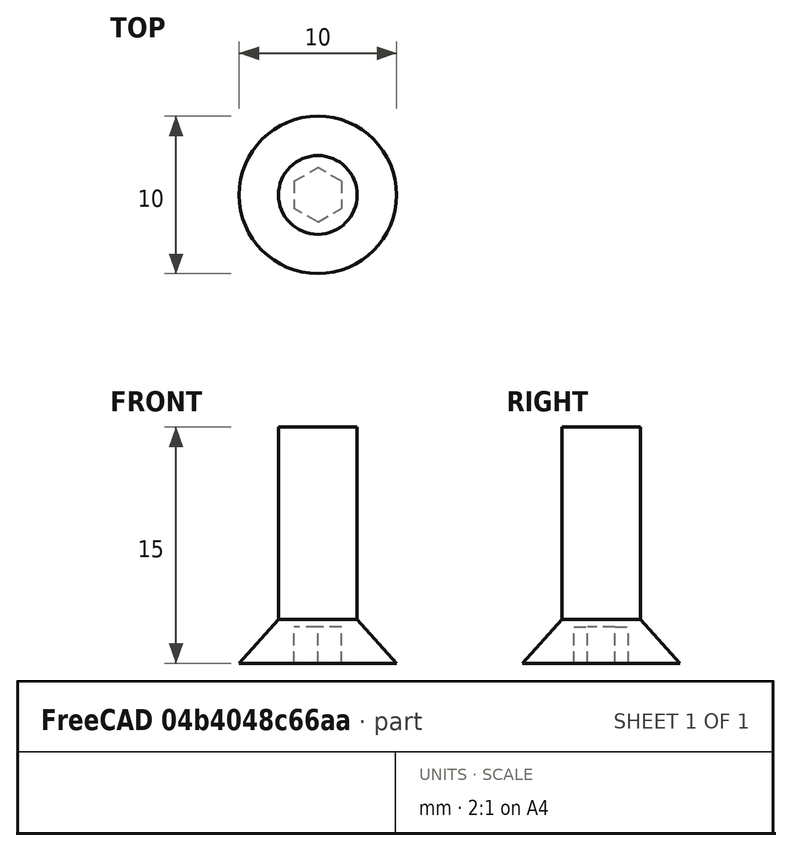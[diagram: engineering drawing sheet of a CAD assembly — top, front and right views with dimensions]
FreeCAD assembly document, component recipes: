
FREECAD ASSEMBLY — COMPONENT RECIPES ("dbox_asm")

This assembly document has 117 components, labeled P0..P116 below (a component is one placed body or linked part). 16 of them carry a construction recipe — the FreeCAD feature program that regenerates the part from scratch, quoted from this document or its linked companion documents; the rest are supplied as boundary geometry only. No exploded tour is included for this assembly.
COMPONENT P0 — recipe-attached ("corner1", a linked part whose construction recipe lives in a companion FreeCAD document of the same project; that document's serialized recipe follows).
Construction recipe (the companion document, serialized — sketch geometry with constraints, then the solid features built on it; lengths are millimeters unless a unit is written):

FCSTD DOCUMENT  (FreeCAD 1.0R39109 (Git))
Label: 2020-corner-bracket
License: All rights reserved
LicenseURL: http://en.wikipedia.org/wiki/All_rights_reserved
objects: Sketcher::SketchObject×5, PartDesign::Pocket×3, PartDesign::Pad×2, PartDesign::PolarPattern×1, PartDesign::Chamfer×1, PartDesign::Body×1, App::Part×1
note: 31 computed .brp shape members not serialized (recipe doc carries the construction recipe); baked Part::Feature solids carry a one-line shape summary decoded from their .brp

FEATURE [Sketcher::SketchObject] Sketch
  ArcFitTolerance = 0
  AttachmentSupport = -> [XZ_Plane001]
  FullyConstrained = true
  MakeInternals = false
  MapMode = 5
  Placement = pos=(0,0,0) rot=(1,0,0;1.5708rad)
  sketch-geometry (5):
    g0: LineSegment StartX=-10 StartY=10 StartZ=0 EndX=-10 EndY=-10 EndZ=0
    g1: LineSegment StartX=-10 StartY=-10 StartZ=0 EndX=10 EndY=-10 EndZ=0
    g2: LineSegment StartX=10 StartY=-10 StartZ=0 EndX=10 EndY=-7 EndZ=0
    g3: LineSegment StartX=10 StartY=-7 StartZ=0 EndX=-7 EndY=10 EndZ=0
    g4: LineSegment StartX=-7 StartY=10 StartZ=0 EndX=-10 EndY=10 EndZ=0
  constraints (13):
    c: Coincident(g0,g1)
    c: Coincident(g1,g2)
    c: Vertical(g2)
    c: Coincident(g2,g3)
    c: Coincident(g3,g4)
    c: Coincident(g4,g0)
    c: Horizontal(g4)
    c: DistanceX(g1,g1) = 20
    c: DistanceY(g2,g2) = 3
    c: Equal(g2,g4)
    c: Equal(g1,g0)
    c: Symmetric(g0,g0,g-1)
    c: Symmetric(g0,g1,g-2)
FEATURE [PartDesign::Pad] Pad
  Direction = (0,-1,2e-16)
  Length = 17
  Length2 = 10
  Midplane = true
  Placement = pos=(0,0,0) rot=(1,0,0;1.5708rad)
  Profile = -> Sketch
  ReferenceAxis = -> Sketch [N_Axis]
  Suppressed = false
  Type = 0
FEATURE [Sketcher::SketchObject] Sketch001
  ArcFitTolerance = 0
  AttachmentSupport = -> [Pad]
  FullyConstrained = true
  MakeInternals = false
  MapMode = 5
  Placement = pos=(-10,0,0) rot=(0.707107,0,-0.707107;3.14159rad)
  sketch-geometry (4):
    g0: ArcOfCircle CenterX=-1.5 CenterY=-2e-16 CenterZ=0 NormalX=0 NormalY=0 NormalZ=1 AngleXU=0 Radius=2.9 StartAngle=1.5708 EndAngle=4.71239
    g1: ArcOfCircle CenterX=1.5 CenterY=-2e-16 CenterZ=0 NormalX=0 NormalY=0 NormalZ=1 AngleXU=0 Radius=2.9 StartAngle=4.71239 EndAngle=7.85398
    g2: LineSegment StartX=-1.5 StartY=-2.9 StartZ=0 EndX=1.5 EndY=-2.9 EndZ=0
    g3: LineSegment StartX=1.5 StartY=2.9 StartZ=0 EndX=-1.5 EndY=2.9 EndZ=0
  constraints (9):
    c: Tangent(g0,g2) = -1.5708
    c: Tangent(g2,g1) = -1.5708
    c: Tangent(g1,g3) = -1.5708
    c: Tangent(g3,g0) = -1.5708
    c: Equal(g0,g1)
    c: DistanceX(g0,g1) = 3
    c: Radius(g0) = 2.9
    c: Symmetric(g1,g0,g-2)
    c: Symmetric(g1,g1,g-1)
FEATURE [PartDesign::Pocket] Pocket
  BaseFeature = -> Pad
  Direction = (1,0,2e-16)
  Length = 3
  Length2 = 5
  Placement = pos=(0,0,0) rot=(1,0,0;1.5708rad)
  Profile = -> Sketch001
  ReferenceAxis = -> Sketch001 [N_Axis]
  Suppressed = false
  Type = 0
FEATURE [Sketcher::SketchObject] Sketch002
  ArcFitTolerance = 0
  AttachmentSupport = -> [Pocket]
  FullyConstrained = true
  MakeInternals = false
  MapMode = 5
  Placement = pos=(0,-4.4e-15,-10) rot=(1,0,0;3.14159rad)
  sketch-geometry (4):
    g0: ArcOfCircle CenterX=-1.5 CenterY=-1e-16 CenterZ=0 NormalX=0 NormalY=0 NormalZ=1 AngleXU=0 Radius=2.9 StartAngle=1.5708 EndAngle=4.71239
    g1: ArcOfCircle CenterX=1.5 CenterY=-1e-16 CenterZ=0 NormalX=0 NormalY=0 NormalZ=1 AngleXU=0 Radius=2.9 StartAngle=4.71239 EndAngle=7.85398
    g2: LineSegment StartX=-1.5 StartY=-2.9 StartZ=0 EndX=1.5 EndY=-2.9 EndZ=0
    g3: LineSegment StartX=1.5 StartY=2.9 StartZ=0 EndX=-1.5 EndY=2.9 EndZ=0
  constraints (9):
    c: Tangent(g0,g2) = -1.5708
    c: Tangent(g2,g1) = -1.5708
    c: Tangent(g1,g3) = -1.5708
    c: Tangent(g3,g0) = -1.5708
    c: Equal(g0,g1)
    c: DistanceX(g0,g1) = 3
    c: Radius(g0) = 2.9
    c: Symmetric(g1,g0,g-2)
    c: Symmetric(g1,g1,g-1)
FEATURE [PartDesign::Pocket] Pocket001
  BaseFeature = -> Pocket
  Direction = (0,0,1)
  Length = 3
  Length2 = 5
  Placement = pos=(0,0,0) rot=(1,0,0;1.5708rad)
  Profile = -> Sketch002
  ReferenceAxis = -> Sketch002 [N_Axis]
  Suppressed = false
  Type = 0
FEATURE [Sketcher::SketchObject] Sketch003
  ArcFitTolerance = 0
  AttachmentSupport = -> [Pocket001]
  ExternalGeometry = -> [Pocket001]
  FullyConstrained = true
  MakeInternals = false
  MapMode = 5
  Placement = pos=(0,0,-7) rot=(1,0,0;3.14159rad)
  sketch-geometry (4):
    g0: LineSegment StartX=-7 StartY=5.5 StartZ=0 EndX=10 EndY=5.5 EndZ=0
    g1: LineSegment StartX=10 StartY=5.5 StartZ=0 EndX=10 EndY=-5.5 EndZ=0
    g2: LineSegment StartX=10 StartY=-5.5 StartZ=0 EndX=-7 EndY=-5.5 EndZ=0
    g3: LineSegment StartX=-7 StartY=-5.5 StartZ=0 EndX=-7 EndY=5.5 EndZ=0
  constraints (11):
    c: Coincident(g0,g1)
    c: Coincident(g1,g2)
    c: Coincident(g2,g3)
    c: Coincident(g3,g0)
    c: Horizontal(g0)
    c: Horizontal(g2)
    c: Vertical(g3)
    c: DistanceY(g3,g3) = 11
    c: Symmetric(g1,g0,g-1)
    c: DistanceX(g0) = -7
    c: DistanceX(g0,g-3) = 0
FEATURE [PartDesign::Pocket] Pocket002
  BaseFeature = -> Pocket001
  Direction = (0,0,1)
  Length = 5
  Length2 = 5
  Placement = pos=(0,0,0) rot=(1,0,0;1.5708rad)
  Profile = -> Sketch003
  ReferenceAxis = -> Sketch003 [N_Axis]
  Suppressed = false
  Type = 1
FEATURE [Sketcher::SketchObject] Sketch004
  ArcFitTolerance = 0
  AttachmentSupport = -> [Pocket002]
  ExternalGeometry = -> [Pocket002]
  FullyConstrained = true
  MakeInternals = false
  MapMode = 5
  Placement = pos=(-10,0,0) rot=(0.707107,0,-0.707107;3.14159rad)
  sketch-geometry (8):
    g0: LineSegment StartX=-8.5 StartY=2 StartZ=0 EndX=-7 EndY=2 EndZ=0
    g1: LineSegment StartX=-7 StartY=2 StartZ=0 EndX=-7 EndY=-2 EndZ=0
    g2: LineSegment StartX=-7 StartY=-2 StartZ=0 EndX=-8.5 EndY=-2 EndZ=0
    g3: LineSegment StartX=-8.5 StartY=-2 StartZ=0 EndX=-8.5 EndY=2 EndZ=0
    g4: LineSegment StartX=7 StartY=2 StartZ=0 EndX=8.5 EndY=2 EndZ=0
    g5: LineSegment StartX=8.5 StartY=2 StartZ=0 EndX=8.5 EndY=-2 EndZ=0
    g6: LineSegment StartX=8.5 StartY=-2 StartZ=0 EndX=7 EndY=-2 EndZ=0
    g7: LineSegment StartX=7 StartY=-2 StartZ=0 EndX=7 EndY=2 EndZ=0
  constraints (23):
    c: Coincident(g0,g1)
    c: Coincident(g1,g2)
    c: Coincident(g2,g3)
    c: Coincident(g3,g0)
    c: Horizontal(g0)
    c: Horizontal(g2)
    c: Vertical(g1)
    c: Vertical(g3)
    c: Coincident(g4,g5)
    c: Coincident(g5,g6)
    c: Coincident(g6,g7)
    c: Coincident(g7,g4)
    c: Horizontal(g4)
    c: Horizontal(g6)
    c: Vertical(g7)
    c: Equal(g5,g1)
    c: Equal(g2,g6)
    c: DistanceX(g0,g0) = 1.5
    c: Horizontal(g1,g6)
    c: Symmetric(g5,g4,g-1)
    c: DistanceX(g4,g-3) = 1.5
    c: DistanceY(g1,g1) = 4
    c: DistanceX(g-4,g0) = 1.5
FEATURE [PartDesign::Pad] Pad001
  BaseFeature = -> Pocket002
  Direction = (-1,0,-2e-16)
  Length = 1
  Length2 = 10
  Placement = pos=(0,0,0) rot=(1,0,0;1.5708rad)
  Profile = -> Sketch004
  ReferenceAxis = -> Sketch004 [N_Axis]
  Suppressed = false
  Type = 0
FEATURE [PartDesign::PolarPattern] PolarPattern
  Angle = 90
  Axis = -> Y_Axis001
  BaseFeature = -> Pad001
  Mode = 0
  Occurrences = 2
  Offset = 120
  Originals = -> [Pad001]
  Placement = pos=(0,0,0) rot=(1,0,0;1.5708rad)
  Reversed = true
  Suppressed = false
  TransformMode = 0
FEATURE [PartDesign::Chamfer] Chamfer
  Angle = 45
  Base = -> PolarPattern [Edge48,Edge45,Edge64,Edge61,Edge80,Edge77,Edge96,Edge93]
  BaseFeature = -> PolarPattern
  ChamferType = 0
  FlipDirection = false
  Placement = pos=(0,0,0) rot=(1,0,0;1.5708rad)
  Size = 0.25
  Size2 = 1
  SupportTransform = false
  Suppressed = false
  UseAllEdges = false
FEATURE [PartDesign::Body] Body
  AllowCompound = false
  Group = -> [Sketch,Pad,Sketch001,Pocket,Sketch002,Pocket001,Sketch003,Pocket002,Sketch004,Pad001,PolarPattern,Chamfer]
  Origin = -> Origin001
  Tip = -> Chamfer
FEATURE [App::Part] Part  label="Part_Bracket"
  Group = -> [Body]
  Origin = -> Origin
COMPONENT P1 — same part as P0; its construction recipe is shown at P0.
COMPONENT P2 — same part as P0; its construction recipe is shown at P0.
COMPONENT P3 — same part as P0; its construction recipe is shown at P0.
COMPONENT P4 — same part as P0; its construction recipe is shown at P0.
COMPONENT P5 — same part as P0; its construction recipe is shown at P0.
COMPONENT P6 — same part as P0; its construction recipe is shown at P0.
COMPONENT P7 — same part as P0; its construction recipe is shown at P0.
COMPONENT P8 — same part as P0; its construction recipe is shown at P0.
COMPONENT P9 — same part as P0; its construction recipe is shown at P0.
COMPONENT P10 — same part as P0; its construction recipe is shown at P0.
COMPONENT P11 — same part as P0; its construction recipe is shown at P0.
COMPONENT P12 — same part as P0; its construction recipe is shown at P0.
COMPONENT P13 — same part as P0; its construction recipe is shown at P0.
COMPONENT P14 — same part as P0; its construction recipe is shown at P0.
COMPONENT P15 — same part as P0; its construction recipe is shown at P0.
COMPONENT P16 — geometry summary ("Hex screw M5 10.008"; no construction recipe available for this part):
  bounding box: 14.0 x 8.5 x 8.5 mm
  tessellated surface: 664 triangles
  volume: 423 mm^3 (42% of its bounding box)
  symmetry: revolution-symmetric about the z axis through its bounding-box center; mirror-symmetric across its x mid-plane, y mid-plane
COMPONENT P17 — geometry summary ("Hex screw M5 10.009"; no construction recipe available for this part):
  bounding box: 14.0 x 8.5 x 8.5 mm
  tessellated surface: 664 triangles
  volume: 423 mm^3 (42% of its bounding box)
  symmetry: revolution-symmetric about the z axis through its bounding-box center; mirror-symmetric across its x mid-plane, y mid-plane
COMPONENT P18 — geometry summary ("Hex screw M5 10.010"; no construction recipe available for this part):
  bounding box: 14.0 x 8.5 x 8.5 mm
  tessellated surface: 664 triangles
  volume: 423 mm^3 (42% of its bounding box)
  symmetry: revolution-symmetric about the z axis through its bounding-box center; mirror-symmetric across its x mid-plane, y mid-plane
COMPONENT P19 — geometry summary ("Hex screw M5 10.011"; no construction recipe available for this part):
  bounding box: 14.0 x 8.5 x 8.5 mm
  tessellated surface: 664 triangles
  volume: 423 mm^3 (42% of its bounding box)
  symmetry: revolution-symmetric about the z axis through its bounding-box center; mirror-symmetric across its x mid-plane, y mid-plane
COMPONENT P20 — geometry summary ("Hex screw M5 10.012"; no construction recipe available for this part):
  bounding box: 14.0 x 8.5 x 8.5 mm
  tessellated surface: 664 triangles
  volume: 423 mm^3 (42% of its bounding box)
  symmetry: revolution-symmetric about the z axis through its bounding-box center; mirror-symmetric across its x mid-plane, y mid-plane
COMPONENT P21 — geometry summary ("Hex screw M5 10.013"; no construction recipe available for this part):
  bounding box: 14.0 x 8.5 x 8.5 mm
  tessellated surface: 664 triangles
  volume: 423 mm^3 (42% of its bounding box)
  symmetry: revolution-symmetric about the z axis through its bounding-box center; mirror-symmetric across its x mid-plane, y mid-plane
COMPONENT P22 — geometry summary ("Hex screw M5 10.014"; no construction recipe available for this part):
  bounding box: 14.0 x 8.5 x 8.5 mm
  tessellated surface: 664 triangles
  volume: 423 mm^3 (42% of its bounding box)
  symmetry: revolution-symmetric about the z axis through its bounding-box center; mirror-symmetric across its x mid-plane, y mid-plane
COMPONENT P23 — geometry summary ("Hex screw M5 10.015"; no construction recipe available for this part):
  bounding box: 14.0 x 8.5 x 8.5 mm
  tessellated surface: 664 triangles
  volume: 423 mm^3 (42% of its bounding box)
  symmetry: revolution-symmetric about the z axis through its bounding-box center; mirror-symmetric across its x mid-plane, y mid-plane
COMPONENT P24 — geometry summary ("Hex screw M5 10.016"; no construction recipe available for this part):
  bounding box: 14.0 x 8.5 x 8.5 mm
  tessellated surface: 664 triangles
  volume: 423 mm^3 (42% of its bounding box)
  symmetry: revolution-symmetric about the z axis through its bounding-box center; mirror-symmetric across its x mid-plane, y mid-plane
COMPONENT P25 — geometry summary ("Hex screw M5 10.017"; no construction recipe available for this part):
  bounding box: 14.0 x 8.5 x 8.5 mm
  tessellated surface: 664 triangles
  volume: 423 mm^3 (42% of its bounding box)
  symmetry: revolution-symmetric about the z axis through its bounding-box center; mirror-symmetric across its x mid-plane, y mid-plane
COMPONENT P26 — geometry summary ("Hex screw M5 10.018"; no construction recipe available for this part):
  bounding box: 14.0 x 8.5 x 8.5 mm
  tessellated surface: 664 triangles
  volume: 423 mm^3 (42% of its bounding box)
  symmetry: revolution-symmetric about the z axis through its bounding-box center; mirror-symmetric across its x mid-plane, y mid-plane
COMPONENT P27 — geometry summary ("Hex screw M5 10.019"; no construction recipe available for this part):
  bounding box: 14.0 x 8.5 x 8.5 mm
  tessellated surface: 664 triangles
  volume: 423 mm^3 (42% of its bounding box)
  symmetry: revolution-symmetric about the z axis through its bounding-box center; mirror-symmetric across its x mid-plane, y mid-plane
COMPONENT P28 — geometry summary ("Hex screw M5 10.020"; no construction recipe available for this part):
  bounding box: 14.0 x 8.5 x 8.5 mm
  tessellated surface: 664 triangles
  volume: 423 mm^3 (42% of its bounding box)
  symmetry: revolution-symmetric about the z axis through its bounding-box center; mirror-symmetric across its x mid-plane, y mid-plane
COMPONENT P29 — geometry summary ("Hex screw M5 10.021"; no construction recipe available for this part):
  bounding box: 14.0 x 8.5 x 8.5 mm
  tessellated surface: 664 triangles
  volume: 423 mm^3 (42% of its bounding box)
  symmetry: revolution-symmetric about the z axis through its bounding-box center; mirror-symmetric across its x mid-plane, y mid-plane
COMPONENT P30 — geometry summary ("Hex screw M5 10.022"; no construction recipe available for this part):
  bounding box: 14.0 x 8.5 x 8.5 mm
  tessellated surface: 664 triangles
  volume: 423 mm^3 (42% of its bounding box)
  symmetry: revolution-symmetric about the z axis through its bounding-box center; mirror-symmetric across its x mid-plane, y mid-plane
COMPONENT P31 — geometry summary ("Hex screw M5 10.023"; no construction recipe available for this part):
  bounding box: 14.0 x 8.5 x 8.5 mm
  tessellated surface: 664 triangles
  volume: 423 mm^3 (42% of its bounding box)
  symmetry: revolution-symmetric about the z axis through its bounding-box center; mirror-symmetric across its x mid-plane, y mid-plane
COMPONENT P32 — geometry summary ("Hex screw M5 10.024"; no construction recipe available for this part):
  bounding box: 14.0 x 8.5 x 8.5 mm
  tessellated surface: 664 triangles
  volume: 423 mm^3 (42% of its bounding box)
  symmetry: revolution-symmetric about the z axis through its bounding-box center; mirror-symmetric across its x mid-plane, y mid-plane
COMPONENT P33 — geometry summary ("Hex screw M5 10.025"; no construction recipe available for this part):
  bounding box: 14.0 x 8.5 x 8.5 mm
  tessellated surface: 664 triangles
  volume: 423 mm^3 (42% of its bounding box)
  symmetry: revolution-symmetric about the z axis through its bounding-box center; mirror-symmetric across its x mid-plane, y mid-plane
COMPONENT P34 — geometry summary ("Hex screw M5 10.026"; no construction recipe available for this part):
  bounding box: 14.0 x 8.5 x 8.5 mm
  tessellated surface: 664 triangles
  volume: 423 mm^3 (42% of its bounding box)
  symmetry: revolution-symmetric about the z axis through its bounding-box center; mirror-symmetric across its x mid-plane, y mid-plane
COMPONENT P35 — geometry summary ("Hex screw M5 10.028"; no construction recipe available for this part):
  bounding box: 14.0 x 8.5 x 8.5 mm
  tessellated surface: 664 triangles
  volume: 423 mm^3 (42% of its bounding box)
  symmetry: revolution-symmetric about the z axis through its bounding-box center; mirror-symmetric across its x mid-plane, y mid-plane
COMPONENT P36 — geometry summary ("Hex screw M5 10.027"; no construction recipe available for this part):
  bounding box: 14.0 x 8.5 x 8.5 mm
  tessellated surface: 664 triangles
  volume: 423 mm^3 (42% of its bounding box)
  symmetry: revolution-symmetric about the z axis through its bounding-box center; mirror-symmetric across its x mid-plane, y mid-plane
COMPONENT P37 — geometry summary ("Hex screw M5 10.029"; no construction recipe available for this part):
  bounding box: 14.0 x 8.5 x 8.5 mm
  tessellated surface: 664 triangles
  volume: 423 mm^3 (42% of its bounding box)
  symmetry: revolution-symmetric about the z axis through its bounding-box center; mirror-symmetric across its x mid-plane, y mid-plane
COMPONENT P38 — geometry summary ("Hex screw M5 10.030"; no construction recipe available for this part):
  bounding box: 14.0 x 8.5 x 8.5 mm
  tessellated surface: 664 triangles
  volume: 423 mm^3 (42% of its bounding box)
  symmetry: revolution-symmetric about the z axis through its bounding-box center; mirror-symmetric across its x mid-plane, y mid-plane
COMPONENT P39 — geometry summary ("Hex screw M5 10.031"; no construction recipe available for this part):
  bounding box: 14.0 x 8.5 x 8.5 mm
  tessellated surface: 664 triangles
  volume: 423 mm^3 (42% of its bounding box)
  symmetry: revolution-symmetric about the z axis through its bounding-box center; mirror-symmetric across its x mid-plane, y mid-plane
COMPONENT P40 — geometry summary ("Hex screw M5 10.032"; no construction recipe available for this part):
  bounding box: 14.0 x 8.5 x 8.5 mm
  tessellated surface: 664 triangles
  volume: 423 mm^3 (42% of its bounding box)
  symmetry: revolution-symmetric about the z axis through its bounding-box center; mirror-symmetric across its x mid-plane, y mid-plane
COMPONENT P41 — geometry summary ("Hex screw M5 10.033"; no construction recipe available for this part):
  bounding box: 14.0 x 8.5 x 8.5 mm
  tessellated surface: 664 triangles
  volume: 423 mm^3 (42% of its bounding box)
  symmetry: revolution-symmetric about the z axis through its bounding-box center; mirror-symmetric across its x mid-plane, y mid-plane
COMPONENT P42 — geometry summary ("Hex screw M5 10.034"; no construction recipe available for this part):
  bounding box: 14.0 x 8.5 x 8.5 mm
  tessellated surface: 664 triangles
  volume: 423 mm^3 (42% of its bounding box)
  symmetry: revolution-symmetric about the z axis through its bounding-box center; mirror-symmetric across its x mid-plane, y mid-plane
COMPONENT P43 — geometry summary ("Hex screw M5 10.035"; no construction recipe available for this part):
  bounding box: 14.0 x 8.5 x 8.5 mm
  tessellated surface: 664 triangles
  volume: 423 mm^3 (42% of its bounding box)
  symmetry: revolution-symmetric about the z axis through its bounding-box center; mirror-symmetric across its x mid-plane, y mid-plane
COMPONENT P44 — geometry summary ("Hex screw M5 10.036"; no construction recipe available for this part):
  bounding box: 14.0 x 8.5 x 8.5 mm
  tessellated surface: 664 triangles
  volume: 423 mm^3 (42% of its bounding box)
  symmetry: revolution-symmetric about the z axis through its bounding-box center; mirror-symmetric across its x mid-plane, y mid-plane
COMPONENT P45 — geometry summary ("Hex screw M5 10.037"; no construction recipe available for this part):
  bounding box: 14.0 x 8.5 x 8.5 mm
  tessellated surface: 664 triangles
  volume: 423 mm^3 (42% of its bounding box)
  symmetry: revolution-symmetric about the z axis through its bounding-box center; mirror-symmetric across its x mid-plane, y mid-plane
COMPONENT P46 — geometry summary ("Hex screw M5 10.038"; no construction recipe available for this part):
  bounding box: 14.0 x 8.5 x 8.5 mm
  tessellated surface: 664 triangles
  volume: 423 mm^3 (42% of its bounding box)
  symmetry: revolution-symmetric about the z axis through its bounding-box center; mirror-symmetric across its x mid-plane, y mid-plane
COMPONENT P47 — geometry summary ("Hex screw M5 10.039"; no construction recipe available for this part):
  bounding box: 14.0 x 8.5 x 8.5 mm
  tessellated surface: 664 triangles
  volume: 423 mm^3 (42% of its bounding box)
  symmetry: revolution-symmetric about the z axis through its bounding-box center; mirror-symmetric across its x mid-plane, y mid-plane
COMPONENT P48 — geometry summary ("Hex screw M5 10.040"; no construction recipe available for this part):
  bounding box: 14.0 x 8.5 x 8.5 mm
  tessellated surface: 664 triangles
  volume: 423 mm^3 (42% of its bounding box)
  symmetry: revolution-symmetric about the z axis through its bounding-box center; mirror-symmetric across its x mid-plane, y mid-plane
COMPONENT P49 — geometry summary ("T-Nut_2020_M006"; no construction recipe available for this part):
  bounding box: 10.5 x 10.0 x 5.0 mm
  tessellated surface: 992 triangles
  volume: 333 mm^3 (63% of its bounding box)
  symmetry: 2-fold rotationally symmetric about the y axis; mirror-symmetric across its x mid-plane, z mid-plane
COMPONENT P50 — geometry summary ("T-Nut_2020_M007"; no construction recipe available for this part):
  bounding box: 10.5 x 10.0 x 5.0 mm
  tessellated surface: 992 triangles
  volume: 333 mm^3 (63% of its bounding box)
  symmetry: 2-fold rotationally symmetric about the y axis; mirror-symmetric across its x mid-plane, z mid-plane
COMPONENT P51 — geometry summary ("T-Nut_2020_M008"; no construction recipe available for this part):
  bounding box: 10.5 x 10.0 x 5.0 mm
  tessellated surface: 992 triangles
  volume: 333 mm^3 (63% of its bounding box)
  symmetry: 2-fold rotationally symmetric about the y axis; mirror-symmetric across its x mid-plane, z mid-plane
COMPONENT P52 — geometry summary ("T-Nut_2020_M009"; no construction recipe available for this part):
  bounding box: 10.5 x 10.0 x 5.0 mm
  tessellated surface: 992 triangles
  volume: 333 mm^3 (63% of its bounding box)
  symmetry: 2-fold rotationally symmetric about the y axis; mirror-symmetric across its x mid-plane, z mid-plane
COMPONENT P53 — geometry summary ("T-Nut_2020_M010"; no construction recipe available for this part):
  bounding box: 10.5 x 10.0 x 5.0 mm
  tessellated surface: 992 triangles
  volume: 333 mm^3 (63% of its bounding box)
  symmetry: 2-fold rotationally symmetric about the y axis; mirror-symmetric across its x mid-plane, z mid-plane
COMPONENT P54 — geometry summary ("T-Nut_2020_M011"; no construction recipe available for this part):
  bounding box: 10.5 x 10.0 x 5.0 mm
  tessellated surface: 992 triangles
  volume: 333 mm^3 (63% of its bounding box)
  symmetry: 2-fold rotationally symmetric about the y axis; mirror-symmetric across its x mid-plane, z mid-plane
COMPONENT P55 — geometry summary ("T-Nut_2020_M012"; no construction recipe available for this part):
  bounding box: 10.5 x 10.0 x 5.0 mm
  tessellated surface: 992 triangles
  volume: 333 mm^3 (63% of its bounding box)
  symmetry: 2-fold rotationally symmetric about the y axis; mirror-symmetric across its x mid-plane, z mid-plane
COMPONENT P56 — geometry summary ("T-Nut_2020_M013"; no construction recipe available for this part):
  bounding box: 10.5 x 10.0 x 5.0 mm
  tessellated surface: 992 triangles
  volume: 333 mm^3 (63% of its bounding box)
  symmetry: 2-fold rotationally symmetric about the y axis; mirror-symmetric across its x mid-plane, z mid-plane
COMPONENT P57 — geometry summary ("T-Nut_2020_M014"; no construction recipe available for this part):
  bounding box: 10.5 x 10.0 x 5.0 mm
  tessellated surface: 992 triangles
  volume: 333 mm^3 (63% of its bounding box)
  symmetry: 2-fold rotationally symmetric about the y axis; mirror-symmetric across its x mid-plane, z mid-plane
COMPONENT P58 — geometry summary ("T-Nut_2020_M015"; no construction recipe available for this part):
  bounding box: 10.5 x 10.0 x 5.0 mm
  tessellated surface: 992 triangles
  volume: 333 mm^3 (63% of its bounding box)
  symmetry: 2-fold rotationally symmetric about the y axis; mirror-symmetric across its x mid-plane, z mid-plane
COMPONENT P59 — geometry summary ("T-Nut_2020_M016"; no construction recipe available for this part):
  bounding box: 10.5 x 10.0 x 5.0 mm
  tessellated surface: 992 triangles
  volume: 333 mm^3 (63% of its bounding box)
  symmetry: 2-fold rotationally symmetric about the y axis; mirror-symmetric across its x mid-plane, z mid-plane
COMPONENT P60 — geometry summary ("T-Nut_2020_M017"; no construction recipe available for this part):
  bounding box: 10.5 x 10.0 x 5.0 mm
  tessellated surface: 992 triangles
  volume: 333 mm^3 (63% of its bounding box)
  symmetry: 2-fold rotationally symmetric about the y axis; mirror-symmetric across its x mid-plane, z mid-plane
COMPONENT P61 — geometry summary ("T-Nut_2020_M018"; no construction recipe available for this part):
  bounding box: 10.5 x 10.0 x 5.0 mm
  tessellated surface: 992 triangles
  volume: 333 mm^3 (63% of its bounding box)
  symmetry: 2-fold rotationally symmetric about the y axis; mirror-symmetric across its x mid-plane, z mid-plane
COMPONENT P62 — geometry summary ("T-Nut_2020_M019"; no construction recipe available for this part):
  bounding box: 10.5 x 10.0 x 5.0 mm
  tessellated surface: 992 triangles
  volume: 333 mm^3 (63% of its bounding box)
  symmetry: 2-fold rotationally symmetric about the y axis; mirror-symmetric across its x mid-plane, z mid-plane
COMPONENT P63 — geometry summary ("T-Nut_2020_M020"; no construction recipe available for this part):
  bounding box: 10.5 x 10.0 x 5.0 mm
  tessellated surface: 992 triangles
  volume: 333 mm^3 (63% of its bounding box)
  symmetry: 2-fold rotationally symmetric about the y axis; mirror-symmetric across its x mid-plane, z mid-plane
COMPONENT P64 — geometry summary ("T-Nut_2020_M021"; no construction recipe available for this part):
  bounding box: 10.5 x 10.0 x 5.0 mm
  tessellated surface: 992 triangles
  volume: 333 mm^3 (63% of its bounding box)
  symmetry: 2-fold rotationally symmetric about the y axis; mirror-symmetric across its x mid-plane, z mid-plane
COMPONENT P65 — geometry summary ("T-Nut_2020_M022"; no construction recipe available for this part):
  bounding box: 10.5 x 10.0 x 5.0 mm
  tessellated surface: 992 triangles
  volume: 333 mm^3 (63% of its bounding box)
  symmetry: 2-fold rotationally symmetric about the y axis; mirror-symmetric across its x mid-plane, z mid-plane
COMPONENT P66 — geometry summary ("T-Nut_2020_M023"; no construction recipe available for this part):
  bounding box: 10.5 x 10.0 x 5.0 mm
  tessellated surface: 992 triangles
  volume: 333 mm^3 (63% of its bounding box)
  symmetry: 2-fold rotationally symmetric about the y axis; mirror-symmetric across its x mid-plane, z mid-plane
COMPONENT P67 — geometry summary ("T-Nut_2020_M024"; no construction recipe available for this part):
  bounding box: 10.5 x 10.0 x 5.0 mm
  tessellated surface: 992 triangles
  volume: 333 mm^3 (63% of its bounding box)
  symmetry: 2-fold rotationally symmetric about the y axis; mirror-symmetric across its x mid-plane, z mid-plane
COMPONENT P68 — geometry summary ("T-Nut_2020_M025"; no construction recipe available for this part):
  bounding box: 10.5 x 10.0 x 5.0 mm
  tessellated surface: 992 triangles
  volume: 333 mm^3 (63% of its bounding box)
  symmetry: 2-fold rotationally symmetric about the y axis; mirror-symmetric across its x mid-plane, z mid-plane
COMPONENT P69 — geometry summary ("T-Nut_2020_M026"; no construction recipe available for this part):
  bounding box: 10.5 x 10.0 x 5.0 mm
  tessellated surface: 992 triangles
  volume: 333 mm^3 (63% of its bounding box)
  symmetry: 2-fold rotationally symmetric about the y axis; mirror-symmetric across its x mid-plane, z mid-plane
COMPONENT P70 — geometry summary ("T-Nut_2020_M027"; no construction recipe available for this part):
  bounding box: 10.5 x 10.0 x 5.0 mm
  tessellated surface: 992 triangles
  volume: 333 mm^3 (63% of its bounding box)
  symmetry: 2-fold rotationally symmetric about the y axis; mirror-symmetric across its x mid-plane, z mid-plane
COMPONENT P71 — geometry summary ("T-Nut_2020_M028"; no construction recipe available for this part):
  bounding box: 10.5 x 10.0 x 5.0 mm
  tessellated surface: 992 triangles
  volume: 333 mm^3 (63% of its bounding box)
  symmetry: 2-fold rotationally symmetric about the y axis; mirror-symmetric across its x mid-plane, z mid-plane
COMPONENT P72 — geometry summary ("T-Nut_2020_M029"; no construction recipe available for this part):
  bounding box: 10.5 x 10.0 x 5.0 mm
  tessellated surface: 992 triangles
  volume: 333 mm^3 (63% of its bounding box)
  symmetry: 2-fold rotationally symmetric about the y axis; mirror-symmetric across its x mid-plane, z mid-plane
COMPONENT P73 — geometry summary ("T-Nut_2020_M030"; no construction recipe available for this part):
  bounding box: 10.5 x 10.0 x 5.0 mm
  tessellated surface: 992 triangles
  volume: 333 mm^3 (63% of its bounding box)
  symmetry: 2-fold rotationally symmetric about the y axis; mirror-symmetric across its x mid-plane, z mid-plane
COMPONENT P74 — geometry summary ("T-Nut_2020_M031"; no construction recipe available for this part):
  bounding box: 10.5 x 10.0 x 5.0 mm
  tessellated surface: 992 triangles
  volume: 333 mm^3 (63% of its bounding box)
  symmetry: 2-fold rotationally symmetric about the y axis; mirror-symmetric across its x mid-plane, z mid-plane
COMPONENT P75 — geometry summary ("T-Nut_2020_M032"; no construction recipe available for this part):
  bounding box: 10.5 x 10.0 x 5.0 mm
  tessellated surface: 992 triangles
  volume: 333 mm^3 (63% of its bounding box)
  symmetry: 2-fold rotationally symmetric about the y axis; mirror-symmetric across its x mid-plane, z mid-plane
COMPONENT P76 — geometry summary ("T-Nut_2020_M033"; no construction recipe available for this part):
  bounding box: 10.5 x 10.0 x 5.0 mm
  tessellated surface: 992 triangles
  volume: 333 mm^3 (63% of its bounding box)
  symmetry: 2-fold rotationally symmetric about the y axis; mirror-symmetric across its x mid-plane, z mid-plane
COMPONENT P77 — geometry summary ("T-Nut_2020_M034"; no construction recipe available for this part):
  bounding box: 10.5 x 10.0 x 5.0 mm
  tessellated surface: 992 triangles
  volume: 333 mm^3 (63% of its bounding box)
  symmetry: 2-fold rotationally symmetric about the y axis; mirror-symmetric across its x mid-plane, z mid-plane
COMPONENT P78 — geometry summary ("T-Nut_2020_M035"; no construction recipe available for this part):
  bounding box: 10.5 x 10.0 x 5.0 mm
  tessellated surface: 992 triangles
  volume: 333 mm^3 (63% of its bounding box)
  symmetry: 2-fold rotationally symmetric about the y axis; mirror-symmetric across its x mid-plane, z mid-plane
COMPONENT P79 — geometry summary ("T-Nut_2020_M036"; no construction recipe available for this part):
  bounding box: 10.5 x 10.0 x 5.0 mm
  tessellated surface: 992 triangles
  volume: 333 mm^3 (63% of its bounding box)
  symmetry: 2-fold rotationally symmetric about the y axis; mirror-symmetric across its x mid-plane, z mid-plane
COMPONENT P80 — geometry summary ("T-Nut_2020_M037"; no construction recipe available for this part):
  bounding box: 10.5 x 10.0 x 5.0 mm
  tessellated surface: 992 triangles
  volume: 333 mm^3 (63% of its bounding box)
  symmetry: 2-fold rotationally symmetric about the y axis; mirror-symmetric across its x mid-plane, z mid-plane
COMPONENT P81 — geometry summary ("T-Nut_2020_M038"; no construction recipe available for this part):
  bounding box: 10.5 x 10.0 x 5.0 mm
  tessellated surface: 992 triangles
  volume: 333 mm^3 (63% of its bounding box)
  symmetry: 2-fold rotationally symmetric about the y axis; mirror-symmetric across its x mid-plane, z mid-plane
COMPONENT P82 — geometry summary ("T-Nut_2020_M039"; no construction recipe available for this part):
  bounding box: 10.5 x 10.0 x 5.0 mm
  tessellated surface: 992 triangles
  volume: 333 mm^3 (63% of its bounding box)
  symmetry: 2-fold rotationally symmetric about the y axis; mirror-symmetric across its x mid-plane, z mid-plane
COMPONENT P83 — geometry summary ("T-Nut_2020_M040"; no construction recipe available for this part):
  bounding box: 10.5 x 10.0 x 5.0 mm
  tessellated surface: 992 triangles
  volume: 333 mm^3 (63% of its bounding box)
  symmetry: 2-fold rotationally symmetric about the y axis; mirror-symmetric across its x mid-plane, z mid-plane
COMPONENT P84 — geometry summary ("T-Nut_2020_M041"; no construction recipe available for this part):
  bounding box: 10.5 x 10.0 x 5.0 mm
  tessellated surface: 992 triangles
  volume: 333 mm^3 (63% of its bounding box)
  symmetry: 2-fold rotationally symmetric about the y axis; mirror-symmetric across its x mid-plane, z mid-plane
COMPONENT P85 — geometry summary ("T-Nut_2020_M042"; no construction recipe available for this part):
  bounding box: 10.5 x 10.0 x 5.0 mm
  tessellated surface: 992 triangles
  volume: 333 mm^3 (63% of its bounding box)
  symmetry: 2-fold rotationally symmetric about the y axis; mirror-symmetric across its x mid-plane, z mid-plane
COMPONENT P86 — geometry summary ("T-Nut_2020_M043"; no construction recipe available for this part):
  bounding box: 10.5 x 10.0 x 5.0 mm
  tessellated surface: 992 triangles
  volume: 333 mm^3 (63% of its bounding box)
  symmetry: 2-fold rotationally symmetric about the y axis; mirror-symmetric across its x mid-plane, z mid-plane
COMPONENT P87 — geometry summary ("T-Nut_2020_M044"; no construction recipe available for this part):
  bounding box: 10.5 x 10.0 x 5.0 mm
  tessellated surface: 992 triangles
  volume: 333 mm^3 (63% of its bounding box)
  symmetry: 2-fold rotationally symmetric about the y axis; mirror-symmetric across its x mid-plane, z mid-plane
COMPONENT P88 — geometry summary ("T-Nut_2020_M045"; no construction recipe available for this part):
  bounding box: 10.5 x 10.0 x 5.0 mm
  tessellated surface: 992 triangles
  volume: 333 mm^3 (63% of its bounding box)
  symmetry: 2-fold rotationally symmetric about the y axis; mirror-symmetric across its x mid-plane, z mid-plane
COMPONENT P89 — geometry summary ("T-Nut_2020_M046"; no construction recipe available for this part):
  bounding box: 10.5 x 10.0 x 5.0 mm
  tessellated surface: 992 triangles
  volume: 333 mm^3 (63% of its bounding box)
  symmetry: 2-fold rotationally symmetric about the y axis; mirror-symmetric across its x mid-plane, z mid-plane
COMPONENT P90 — geometry summary ("T-Nut_2020_M047"; no construction recipe available for this part):
  bounding box: 10.5 x 10.0 x 5.0 mm
  tessellated surface: 992 triangles
  volume: 333 mm^3 (63% of its bounding box)
  symmetry: 2-fold rotationally symmetric about the y axis; mirror-symmetric across its x mid-plane, z mid-plane
COMPONENT P91 — geometry summary ("T-Nut_2020_M048"; no construction recipe available for this part):
  bounding box: 10.5 x 10.0 x 5.0 mm
  tessellated surface: 992 triangles
  volume: 333 mm^3 (63% of its bounding box)
  symmetry: 2-fold rotationally symmetric about the y axis; mirror-symmetric across its x mid-plane, z mid-plane
COMPONENT P92 — geometry summary ("T-Nut_2020_M049"; no construction recipe available for this part):
  bounding box: 10.5 x 10.0 x 5.0 mm
  tessellated surface: 992 triangles
  volume: 333 mm^3 (63% of its bounding box)
  symmetry: 2-fold rotationally symmetric about the y axis; mirror-symmetric across its x mid-plane, z mid-plane
COMPONENT P93 — geometry summary ("T-Nut_2020_M050"; no construction recipe available for this part):
  bounding box: 10.5 x 10.0 x 5.0 mm
  tessellated surface: 992 triangles
  volume: 333 mm^3 (63% of its bounding box)
  symmetry: 2-fold rotationally symmetric about the y axis; mirror-symmetric across its x mid-plane, z mid-plane
COMPONENT P94 — geometry summary ("T-Nut_2020_M051"; no construction recipe available for this part):
  bounding box: 10.5 x 10.0 x 5.0 mm
  tessellated surface: 992 triangles
  volume: 333 mm^3 (63% of its bounding box)
  symmetry: 2-fold rotationally symmetric about the y axis; mirror-symmetric across its x mid-plane, z mid-plane
COMPONENT P95 — geometry summary ("T-Nut_2020_M052"; no construction recipe available for this part):
  bounding box: 10.5 x 10.0 x 5.0 mm
  tessellated surface: 992 triangles
  volume: 333 mm^3 (63% of its bounding box)
  symmetry: 2-fold rotationally symmetric about the y axis; mirror-symmetric across its x mid-plane, z mid-plane
COMPONENT P96 — geometry summary ("T-Nut_2020_M053"; no construction recipe available for this part):
  bounding box: 10.5 x 10.0 x 5.0 mm
  tessellated surface: 992 triangles
  volume: 333 mm^3 (63% of its bounding box)
  symmetry: 2-fold rotationally symmetric about the y axis; mirror-symmetric across its x mid-plane, z mid-plane
COMPONENT P97 — geometry summary ("T-Nut_2020_M054"; no construction recipe available for this part):
  bounding box: 10.5 x 10.0 x 5.0 mm
  tessellated surface: 992 triangles
  volume: 333 mm^3 (63% of its bounding box)
  symmetry: 2-fold rotationally symmetric about the y axis; mirror-symmetric across its x mid-plane, z mid-plane
COMPONENT P98 — geometry summary ("T-Nut_2020_M055"; no construction recipe available for this part):
  bounding box: 10.5 x 10.0 x 5.0 mm
  tessellated surface: 992 triangles
  volume: 333 mm^3 (63% of its bounding box)
  symmetry: 2-fold rotationally symmetric about the y axis; mirror-symmetric across its x mid-plane, z mid-plane
COMPONENT P99 — geometry summary ("T-Nut_2020_M056"; no construction recipe available for this part):
  bounding box: 10.5 x 10.0 x 5.0 mm
  tessellated surface: 992 triangles
  volume: 333 mm^3 (63% of its bounding box)
  symmetry: 2-fold rotationally symmetric about the y axis; mirror-symmetric across its x mid-plane, z mid-plane
COMPONENT P100 — geometry summary ("T-Nut_2020_M057"; no construction recipe available for this part):
  bounding box: 10.5 x 10.0 x 5.0 mm
  tessellated surface: 992 triangles
  volume: 333 mm^3 (63% of its bounding box)
  symmetry: 2-fold rotationally symmetric about the y axis; mirror-symmetric across its x mid-plane, z mid-plane
COMPONENT P101 — geometry summary ("T-Nut_2020_M058"; no construction recipe available for this part):
  bounding box: 10.5 x 10.0 x 5.0 mm
  tessellated surface: 992 triangles
  volume: 333 mm^3 (63% of its bounding box)
  symmetry: 2-fold rotationally symmetric about the y axis; mirror-symmetric across its x mid-plane, z mid-plane
COMPONENT P102 — geometry summary ("T-Nut_2020_M059"; no construction recipe available for this part):
  bounding box: 10.5 x 10.0 x 5.0 mm
  tessellated surface: 992 triangles
  volume: 333 mm^3 (63% of its bounding box)
  symmetry: 2-fold rotationally symmetric about the y axis; mirror-symmetric across its x mid-plane, z mid-plane
COMPONENT P103 — geometry summary ("T-Nut_2020_M060"; no construction recipe available for this part):
  bounding box: 10.5 x 10.0 x 5.0 mm
  tessellated surface: 992 triangles
  volume: 333 mm^3 (63% of its bounding box)
  symmetry: 2-fold rotationally symmetric about the y axis; mirror-symmetric across its x mid-plane, z mid-plane
COMPONENT P104 — geometry summary ("T-Nut_2020_M5"; no construction recipe available for this part):
  bounding box: 10.5 x 10.0 x 5.0 mm
  tessellated surface: 992 triangles
  volume: 333 mm^3 (63% of its bounding box)
  symmetry: 2-fold rotationally symmetric about the y axis; mirror-symmetric across its x mid-plane, z mid-plane
COMPONENT P105 — geometry summary ("Tslot20_heigh"; no construction recipe available for this part):
  bounding box: 580.0 x 20.0 x 20.0 mm
  tessellated surface: 392 triangles
  volume: 112281 mm^3 (48% of its bounding box)
  symmetry: 2-fold rotationally symmetric about the x axis; 2-fold rotationally symmetric about the y axis; 4-fold rotationally symmetric about the z axis; mirror-symmetric across its x mid-plane, y mid-plane, z mid-plane
COMPONENT P106 — geometry summary ("Tslot20_heigh001"; no construction recipe available for this part):
  bounding box: 580.0 x 20.0 x 20.0 mm
  tessellated surface: 392 triangles
  volume: 112281 mm^3 (48% of its bounding box)
  symmetry: 2-fold rotationally symmetric about the x axis; 2-fold rotationally symmetric about the y axis; 4-fold rotationally symmetric about the z axis; mirror-symmetric across its x mid-plane, y mid-plane, z mid-plane
COMPONENT P107 — geometry summary ("Tslot20_heigh002"; no construction recipe available for this part):
  bounding box: 580.0 x 20.0 x 20.0 mm
  tessellated surface: 392 triangles
  volume: 112281 mm^3 (48% of its bounding box)
  symmetry: 2-fold rotationally symmetric about the x axis; 2-fold rotationally symmetric about the y axis; 4-fold rotationally symmetric about the z axis; mirror-symmetric across its x mid-plane, y mid-plane, z mid-plane
COMPONENT P108 — geometry summary ("Tslot20_heigh003"; no construction recipe available for this part):
  bounding box: 580.0 x 20.0 x 20.0 mm
  tessellated surface: 392 triangles
  volume: 112281 mm^3 (48% of its bounding box)
  symmetry: 2-fold rotationally symmetric about the x axis; 2-fold rotationally symmetric about the y axis; 4-fold rotationally symmetric about the z axis; mirror-symmetric across its x mid-plane, y mid-plane, z mid-plane
COMPONENT P109 — geometry summary ("Tslot20_len"; no construction recipe available for this part):
  bounding box: 400.0 x 20.0 x 20.0 mm
  tessellated surface: 392 triangles
  volume: 77435 mm^3 (48% of its bounding box)
  symmetry: 4-fold rotationally symmetric about the x axis; 2-fold rotationally symmetric about the y axis; 2-fold rotationally symmetric about the z axis; mirror-symmetric across its x mid-plane, y mid-plane
COMPONENT P110 — geometry summary ("Tslot20_len001"; no construction recipe available for this part):
  bounding box: 400.0 x 20.0 x 20.0 mm
  tessellated surface: 392 triangles
  volume: 77435 mm^3 (48% of its bounding box)
  symmetry: 4-fold rotationally symmetric about the x axis; 2-fold rotationally symmetric about the y axis; 2-fold rotationally symmetric about the z axis; mirror-symmetric across its x mid-plane, y mid-plane
COMPONENT P111 — geometry summary ("Tslot20_len002"; no construction recipe available for this part):
  bounding box: 400.0 x 20.0 x 20.0 mm
  tessellated surface: 392 triangles
  volume: 77435 mm^3 (48% of its bounding box)
  symmetry: 4-fold rotationally symmetric about the x axis; 2-fold rotationally symmetric about the y axis; 2-fold rotationally symmetric about the z axis; mirror-symmetric across its x mid-plane, y mid-plane
COMPONENT P112 — geometry summary ("Tslot20_len003"; no construction recipe available for this part):
  bounding box: 400.0 x 20.0 x 20.0 mm
  tessellated surface: 392 triangles
  volume: 77435 mm^3 (48% of its bounding box)
  symmetry: 4-fold rotationally symmetric about the x axis; 2-fold rotationally symmetric about the y axis; 2-fold rotationally symmetric about the z axis; mirror-symmetric across its x mid-plane, y mid-plane
COMPONENT P113 — geometry summary ("Tslot20_wid"; no construction recipe available for this part):
  bounding box: 200.0 x 20.0 x 20.0 mm
  tessellated surface: 392 triangles
  volume: 38718 mm^3 (48% of its bounding box)
  symmetry: 4-fold rotationally symmetric about the y axis; mirror-symmetric across its x mid-plane, y mid-plane, z mid-plane
COMPONENT P114 — geometry summary ("Tslot20_wid001"; no construction recipe available for this part):
  bounding box: 200.0 x 20.0 x 20.0 mm
  tessellated surface: 392 triangles
  volume: 38718 mm^3 (48% of its bounding box)
  symmetry: 4-fold rotationally symmetric about the y axis; mirror-symmetric across its x mid-plane, y mid-plane, z mid-plane
COMPONENT P115 — geometry summary ("Tslot20_wid002"; no construction recipe available for this part):
  bounding box: 200.0 x 20.0 x 20.0 mm
  tessellated surface: 392 triangles
  volume: 38718 mm^3 (48% of its bounding box)
  symmetry: 4-fold rotationally symmetric about the y axis; mirror-symmetric across its x mid-plane, y mid-plane, z mid-plane
COMPONENT P116 — geometry summary ("Tslot20_wid003"; no construction recipe available for this part):
  bounding box: 200.0 x 20.0 x 20.0 mm
  tessellated surface: 392 triangles
  volume: 38718 mm^3 (48% of its bounding box)
  symmetry: 4-fold rotationally symmetric about the y axis; mirror-symmetric across its x mid-plane, y mid-plane, z mid-plane
PROVENANCE & LICENSES
A FreeCAD (.FCStd) document from a public repository crawl; recipes are the document's own serialized feature recipes (and, for linked parts, companion documents' recipes).
License: as declared in the source repository (recorded in the dataset sidecar).
